# Revit family: Table_MARK_Type Focus_ 6Booth_3300x1200-Rev2
name_source: partatom
category: Furniture
revit_build: Autodesk Revit 2015 (Build: 20140905_0730(x64)
units: mm (PartAtom-declared; Revit-internal decimal feet)

## types (2) — shared parameters
Depth = 1200 mm  [stored 3.93701 ft]
Fillet = 3 mm  [stored 0.00984252 ft]
Frame Width = 50 mm  [stored 0.164042 ft]
Height = 740 mm  [stored 2.42782 ft]
LegHeight = 738 mm
Leg_Offset = 55 mm
Manufacturer = MARK
Manufacturer Adress = Rosemanowes Quarry, Herniss, Penryn,

Cornwall, TR10 9DU
Manufacturer URL = http://www.markproduct.com
MidSepLength = 1057 mm
Model = 1100x3300 mm 6 Booth Type FocusTable System
Model Version = 1
Offset = 20 mm  [stored 0.0656168 ft]
Product Category = Type FocusTable System
Product Color = Available all color
Product Desctription = Type FocusTable System
Revit Version = Revit 2015
URL = http://www.markproduct.com
Width = 3300 mm  [stored 10.8268 ft]

## per-type parameters (varying)
| type | Assembly Code | Fixture Material | Material_Frame | Material_Seperator | Material_TableTop |
| Table 1 | E2020400 | Metal Panel | Metal Panel | Linen, Blue | Linen, Blue_Light |
| MidSepLength | E2020500 | Mark_BALCK | Mark_Orange | Mark_Red5 | Mark_BALCK 2 |

note: [stored X ft] marks values corroborated as IEEE doubles in the binary element streams (Revit-internal decimal feet)

## geometry (parser evidence)
native form markers: Blend x6, Sweep x13
no freeform markers — native parametric forms only
